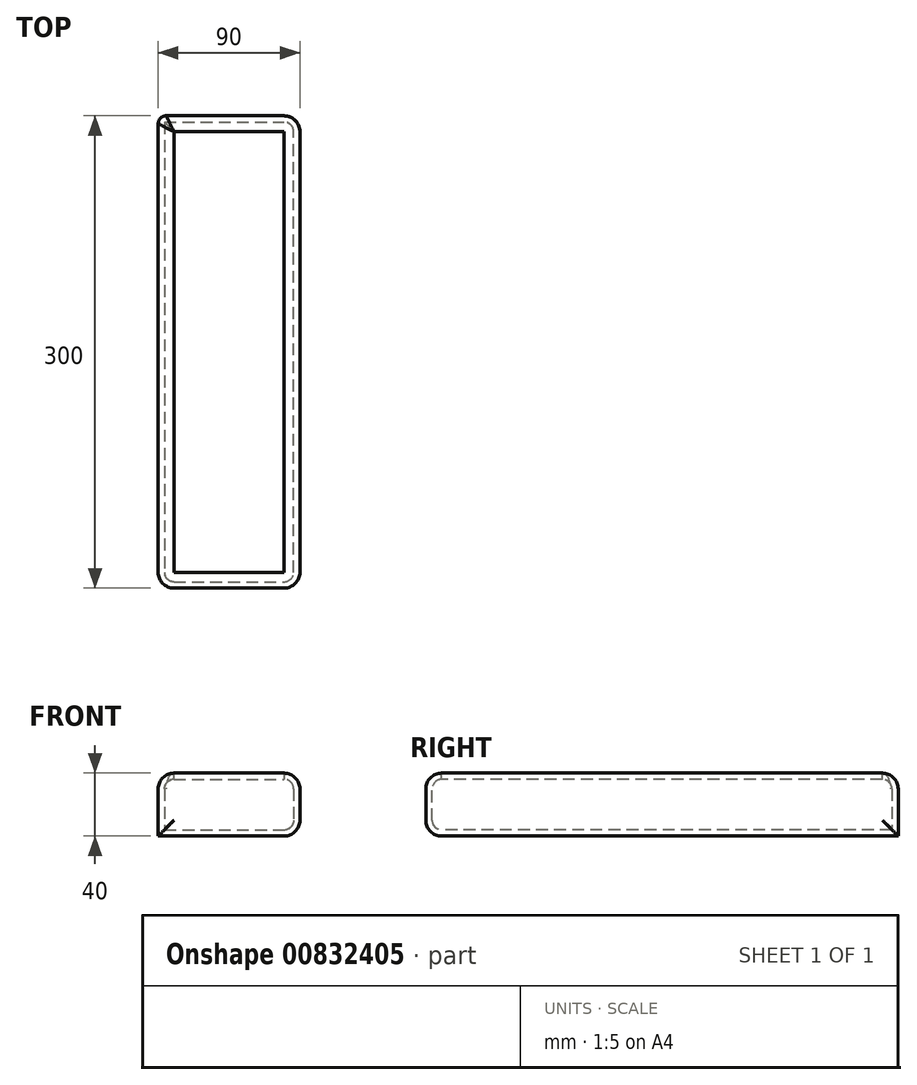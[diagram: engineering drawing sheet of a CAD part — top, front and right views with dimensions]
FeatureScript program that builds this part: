
annotation { "Feature Type Name" : "Feature", "Feature Type Description" : "" }
export const myFeature = defineFeature(function(context is Context, id is Id, definition is map)
    precondition{}
    {
        {
            var Q0;
            Q0=qCreatedBy(makeId("Top.planeOp"),FACE);
            var sketch = newSketch(context, id + "F0", { "sketchPlane" : qUnion([Q0])});
            skLineSegment(sketch, "E0.bottom", {"start": v(75.24, 156.97) * mm, "end": v(165.24, 156.97) * mm});
            skLineSegment(sketch, "E0.top", {"start": v(75.24, -143.03) * mm, "end": v(165.24, -143.03) * mm});
            skLineSegment(sketch, "E0.left", {"start": v(75.24, 156.97) * mm, "end": v(75.24, -143.03) * mm});
            skLineSegment(sketch, "E0.right", {"start": v(165.24, 156.97) * mm, "end": v(165.24, -143.03) * mm});
            skPoint(sketch, "E0.middle", {"position": v(120.24, 6.97) * mm});
            skSolve(sketch);
        }
        {
            var Q0;
            Q0 = qSketchRegion(id + "F0", true);
            extrude(context, id + "F1", {"entities" : qUnion([Q0]), "depth" : 40 * mm, "offsetDistance" : 25 * mm});
        }
        {
            var Q0;
            Q0=makeQuery(id+"F1.opExtrude","CAP_FACE",FACE,{"disambiguationData":[OSD([sQuery(id+"F0.wireOp",EDGE,"E0.bottom"),sQuery(id+"F0.wireOp",EDGE,"E0.top"),sQuery(id+"F0.wireOp",EDGE,"E0.left"),sQuery(id+"F0.wireOp",EDGE,"E0.right")])],"isStart":false});
            var Q1;
            Q1=makeQuery(id+"F1.opExtrude","CAP_EDGE",EDGE,{"disambiguationData":[OSD([sQuery(id+"F0.wireOp",EDGE,"E0.right")])],"isStart":true});
            var Q2;
            Q2=makeQuery(id+"F1.opExtrude","CAP_EDGE",EDGE,{"disambiguationData":[OSD([sQuery(id+"F0.wireOp",EDGE,"E0.top")])],"isStart":true});
            var Q3;
            Q3=makeQuery(id+"F1.opExtrude","SWEPT_EDGE",EDGE,{"disambiguationData":[OSD([sQuery(id+"F0.wireOp",EDGE,"E0.bottom"),sQuery(id+"F0.wireOp",EDGE,"E0.right")])]});
            var Q4;
            Q4=makeQuery(id+"F1.opExtrude","SWEPT_EDGE",EDGE,{"disambiguationData":[OSD([sQuery(id+"F0.wireOp",EDGE,"E0.top"),sQuery(id+"F0.wireOp",EDGE,"E0.right")])]});
            var Q5;
            Q5=makeQuery(id+"F1.opExtrude","SWEPT_EDGE",EDGE,{"disambiguationData":[OSD([sQuery(id+"F0.wireOp",EDGE,"E0.top"),sQuery(id+"F0.wireOp",EDGE,"E0.left")])]});
            fillet(context, id + "F2", {"entities" : qUnion([Q0, Q1, Q2, Q3, Q4, Q5]), "radius" : 10 * mm, "tangentPropagation" : true, "allowEdgeOverflow" : false});
        }
        {
            var Q0;
            Q0=makeQuery(id+"F1.opExtrude","CAP_FACE",FACE,{"disambiguationData":[OSD([sQuery(id+"F0.wireOp",EDGE,"E0.bottom"),sQuery(id+"F0.wireOp",EDGE,"E0.top"),sQuery(id+"F0.wireOp",EDGE,"E0.left"),sQuery(id+"F0.wireOp",EDGE,"E0.right")])],"isStart":false});
            shell(context, id + "F3", {"entities" : qUnion([Q0]), "thickness" : 4 * mm});
        }
        {
            var Q0;
            Q0=makeQuery(id+"F2.opFillet","BLEND_EDGE",EDGE,{"blendedFrom":[makeQuery(id+"F1.opExtrude","CAP_EDGE",EDGE,{"disambiguationData":[OSD([sQuery(id+"F0.wireOp",EDGE,"E0.bottom")])],"isStart":false}),makeQuery(id+"F1.opExtrude","CAP_EDGE",EDGE,{"disambiguationData":[OSD([sQuery(id+"F0.wireOp",EDGE,"E0.left")])],"isStart":false})],"blendedInto":[]});
            fillet(context, id + "F4", {"entities" : qUnion([Q0]), "radius" : 5 * mm, "tangentPropagation" : true, "allowEdgeOverflow" : false});
        }
    });
